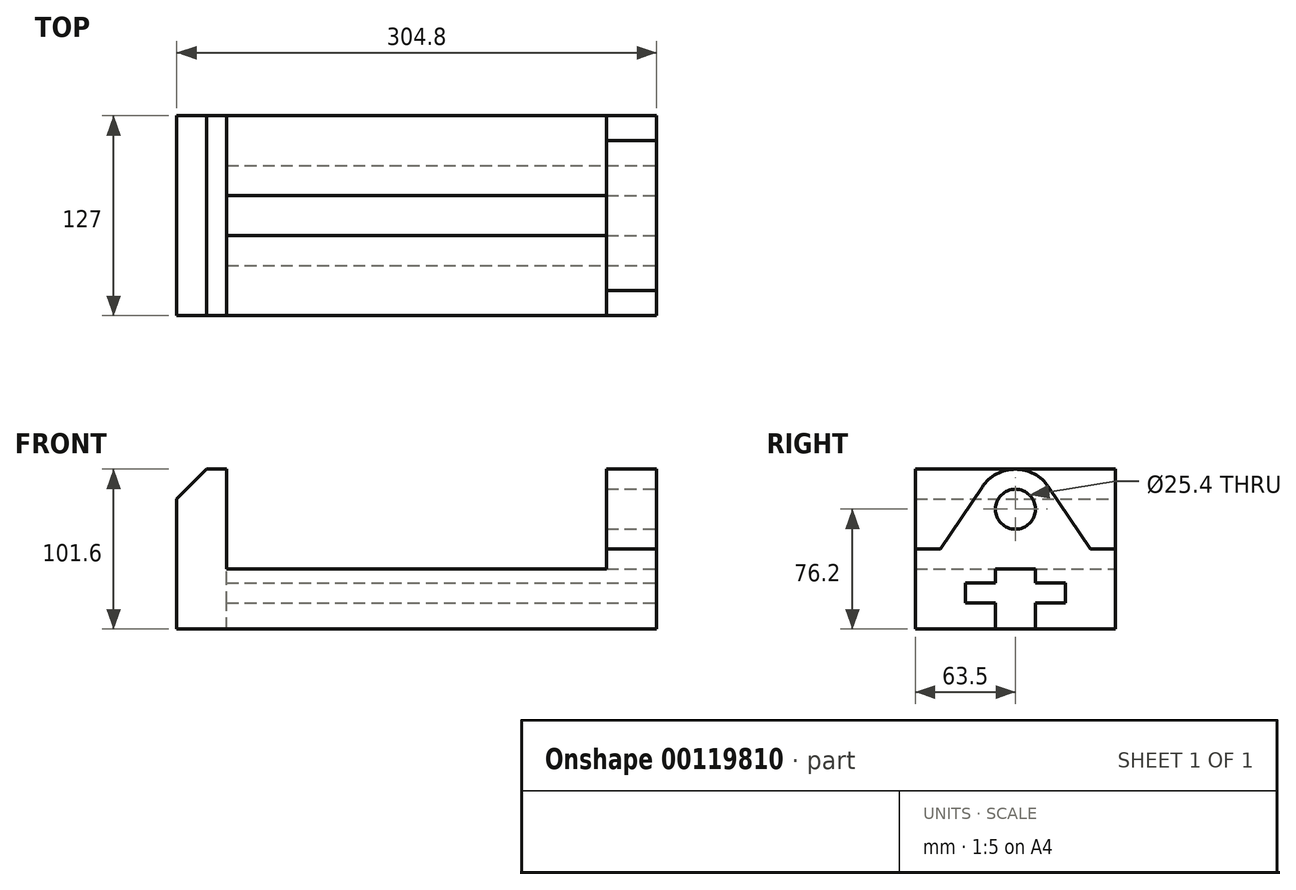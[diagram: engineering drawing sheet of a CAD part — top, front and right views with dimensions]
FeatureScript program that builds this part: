
annotation { "Feature Type Name" : "Feature", "Feature Type Description" : "" }
export const myFeature = defineFeature(function(context is Context, id is Id, definition is map)
    precondition{}
    {
        {
            var Q0;
            Q0=qCreatedBy(makeId("Front.planeOp"),FACE);
            var sketch = newSketch(context, id + "F0", { "sketchPlane" : qUnion([Q0])});
            skLineSegment(sketch, "E0.bottom", {"start": v(0, 0) * mm, "end": v(304.8, 0) * mm});
            skLineSegment(sketch, "E0.top", {"start": v(0, 101.6) * mm, "end": v(304.8, 101.6) * mm});
            skLineSegment(sketch, "E0.left", {"start": v(0, 0) * mm, "end": v(0, 101.6) * mm});
            skLineSegment(sketch, "E0.right", {"start": v(304.8, 0) * mm, "end": v(304.8, 101.6) * mm});
            skLineSegment(sketch, "E1", {"start": v(31.75, 38.1) * mm, "end": v(273.05, 38.1) * mm});
            skLineSegment(sketch, "E2", {"start": v(31.75, 101.6) * mm, "end": v(31.75, 0) * mm});
            skLineSegment(sketch, "E3", {"start": v(273.05, 101.6) * mm, "end": v(273.05, 0) * mm});
            skLineSegment(sketch, "E4", {"start": v(0, 82.55) * mm, "end": v(19.05, 101.6) * mm});
            skSolve(sketch);
        }
        {
            var Q0;
            {var subQ4=sQuery(id+"F0.wireOp",EDGE,"E0.right");Q0=makeQuery(id+"F0.imprint","IMPRINT",FACE,{"disambiguationData":[TD([[makeQuery(id+"F0.imprint","IMPRINT",EDGE,{"derivedFrom":subQ4}),1.0]])]});}
            var Q1;
            {var subQ7=sQuery(id+"F0.wireOp",EDGE,"E4");Q1=makeQuery(id+"F0.imprint","IMPRINT",FACE,{"disambiguationData":[TD([[makeQuery(id+"F0.imprint","IMPRINT",EDGE,{"derivedFrom":subQ7}),-1.0]])]});}
            var Q2;
            {var subQ5=sQuery(id+"F0.wireOp",EDGE,"E1");Q2=makeQuery(id+"F0.imprint","IMPRINT",FACE,{"disambiguationData":[TD([[makeQuery(id+"F0.imprint","IMPRINT",EDGE,{"derivedFrom":subQ5}),-1.0]])]});}
            extrude(context, id + "F1", {"entities" : qUnion([Q0, Q1, Q2]), "endBound" : BoundingType.SYMMETRIC, "depth" : 127 * mm});
        }
        {
            var Q0;
            Q0=makeQuery(id+"F1.opExtrude","SWEPT_FACE",FACE,{"disambiguationData":[OSD([sQuery(id+"F0.wireOp",EDGE,"E0.right")])]});
            var sketch = newSketch(context, id + "F2", { "sketchPlane" : qUnion([Q0])});
            skLineSegment(sketch, "E5", {"start": v(-12.7, 0) * mm, "end": v(12.7, 0) * mm});
            skLineSegment(sketch, "E6", {"start": v(12.7, 0) * mm, "end": v(12.7, 16.51) * mm});
            skLineSegment(sketch, "E7", {"start": v(12.7, 16.5) * mm, "end": v(31.75, 16.5) * mm});
            skLineSegment(sketch, "E8", {"start": v(31.75, 16.51) * mm, "end": v(31.75, 29.21) * mm});
            skLineSegment(sketch, "E9", {"start": v(31.75, 29.21) * mm, "end": v(12.7, 29.21) * mm});
            skLineSegment(sketch, "E10", {"start": v(12.7, 29.21) * mm, "end": v(12.7, 38.1) * mm});
            skLineSegment(sketch, "E11", {"start": v(12.7, 38.1) * mm, "end": v(-12.7, 38.1) * mm});
            skLineSegment(sketch, "E12", {"start": v(-12.7, 38.1) * mm, "end": v(-12.7, 29.2) * mm});
            skLineSegment(sketch, "E13", {"start": v(-12.7, 29.21) * mm, "end": v(-31.75, 29.2) * mm});
            skLineSegment(sketch, "E14", {"start": v(-31.75, 29.21) * mm, "end": v(-31.75, 16.51) * mm});
            skLineSegment(sketch, "E15", {"start": v(-31.75, 16.5) * mm, "end": v(-12.7, 16.51) * mm});
            skLineSegment(sketch, "E16", {"start": v(-12.7, 16.51) * mm, "end": v(-12.7, 0) * mm});
            skLineSegment(sketch, "E17", {"start": v(0, 101.6) * mm, "end": v(0, 0) * mm, "construction": true});
            skLineSegment(sketch, "E18", {"start": v(-63.5, 0) * mm, "end": v(-63.5, 50.8) * mm});
            skLineSegment(sketch, "E19", {"start": v(-63.5, 50.8) * mm, "end": v(-47.62, 50.8) * mm});
            skLineSegment(sketch, "E20", {"start": v(63.5, 0) * mm, "end": v(63.5, 50.8) * mm});
            skLineSegment(sketch, "E21", {"start": v(63.5, 50.8) * mm, "end": v(47.63, 50.8) * mm});
            skCircle(sketch, "E22", {"center": v(0, 76.2) * mm, "radius": 12.7 * mm});
            skLineSegment(sketch, "E23", {"start": v(-47.63, 50.8) * mm, "end": v(-21.1, 90.35) * mm});
            skLineSegment(sketch, "E24", {"start": v(47.63, 50.8) * mm, "end": v(21.1, 90.35) * mm});
            skArc(sketch, "E25", {"start": v(21.1, 90.35) * mm, "mid": v(0, 101.6) * mm, "end": v(-21.1, 90.35) * mm});
            skSolve(sketch);
        }
        {
            var Q0;
            Q0 = qSketchRegion(id + "F2", true);
            var Q1;
            {var subQ5=sQuery(id+"F2.wireOp",EDGE,"E19");Q1=makeQuery(id+"F2.imprint","IMPRINT",FACE,{"disambiguationData":[TD([[makeQuery(id+"F2.imprint","IMPRINT",EDGE,{"derivedFrom":subQ5}),1.0]])]});}
            var Q2;
            {var subQ4=sQuery(id+"F2.wireOp",EDGE,"E21");Q2=makeQuery(id+"F2.imprint","IMPRINT",FACE,{"disambiguationData":[TD([[makeQuery(id+"F2.imprint","IMPRINT",EDGE,{"derivedFrom":subQ4}),-1.0]])]});}
            extrude(context, id + "F3", {"entities" : qUnion([Q0, Q1, Q2]), "operationType" : NewBodyOperationType.REMOVE, "endBound" : BoundingType.UP_TO_NEXT, "oppositeDirection" : true, "depth" : 25.4 * mm});
        }
        {
            var Q0;
            Q0=makeQuery(id+"F1.opExtrude","SWEPT_FACE",FACE,{"disambiguationData":[OSD([sQuery(id+"F0.wireOp",EDGE,"E0.left")])]});
            var sketch = newSketch(context, id + "F4", { "sketchPlane" : qUnion([Q0])});
            skLineSegment(sketch, "E26", {"start": v(-12.7, 0) * mm, "end": v(-12.7, 16.5) * mm});
            skLineSegment(sketch, "E27", {"start": v(-12.7, 16.5) * mm, "end": v(-31.75, 16.5) * mm});
            skLineSegment(sketch, "E28", {"start": v(-31.75, 16.5) * mm, "end": v(-31.75, 29.21) * mm});
            skLineSegment(sketch, "E29", {"start": v(-31.75, 29.21) * mm, "end": v(-12.7, 29.21) * mm});
            skLineSegment(sketch, "E30", {"start": v(-12.7, 29.21) * mm, "end": v(-12.7, 38.1) * mm});
            skLineSegment(sketch, "E31", {"start": v(-12.7, 38.1) * mm, "end": v(12.7, 38.1) * mm});
            skLineSegment(sketch, "E32", {"start": v(12.7, 38.1) * mm, "end": v(12.7, 29.21) * mm});
            skLineSegment(sketch, "E33", {"start": v(12.7, 29.21) * mm, "end": v(31.75, 29.21) * mm});
            skLineSegment(sketch, "E34", {"start": v(31.75, 29.21) * mm, "end": v(31.75, 16.5) * mm});
            skLineSegment(sketch, "E35", {"start": v(31.75, 16.5) * mm, "end": v(12.7, 16.51) * mm});
            skLineSegment(sketch, "E36", {"start": v(12.7, 16.51) * mm, "end": v(12.7, 0) * mm});
            skLineSegment(sketch, "E37", {"start": v(12.7, 0) * mm, "end": v(-12.7, 0) * mm});
            skSolve(sketch);
        }
        {
            var Q0;
            Q0 = qSketchRegion(id + "F4", true);
            extrude(context, id + "F5", {"entities" : qUnion([Q0]), "operationType" : NewBodyOperationType.ADD, "oppositeDirection" : true, "depth" : 31.75 * mm});
        }
    });
